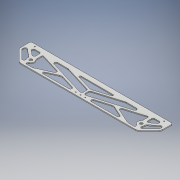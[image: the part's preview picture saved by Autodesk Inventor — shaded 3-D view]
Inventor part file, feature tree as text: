
AUTODESK INVENTOR PART (.ipt)
format: ipt  version: 2018.3 (Build 223284000, 284)  size: 371,712 bytes
history: native  units: mm
features: fillet x20, extrude x5, sketch x4
ambient origin geometry x8: Origin, YZ Plane, XZ Plane, XY Plane, X Axis, Y Axis, Z Axis, Center Point
bodies: Solid1 (feature_tree)
feature tree (29):
  sketch  "Sketch1"  dims[d14=6.0mm d18=6.0mm d19=6.0mm d22=6.0mm d26=37.5mm]
  extrude  "Extrusion1"  Depth=37.5mm
  extrude  "Extrusion2"  Depth=37.5mm
  fillet  "Fillet1"  Radius=3.1mm
  fillet  "Fillet2"  Radius=7.5mm
  fillet  "Fillet3"  Radius=3.1mm
  fillet  "Fillet5"  Radius=7.5mm
  fillet  "Fillet6"  Radius=6.0mm
  fillet  "Fillet7"  Radius=6.0mm
  fillet  "Fillet8"  Radius=3.0mm
  fillet  "Fillet9"  Radius=3.0mm
  fillet  "Fillet10"  Radius=3.0mm
  fillet  "Fillet11"  Radius=3.175mm
  fillet  "Fillet12"  Radius=3.175mm
  extrude  "Extrusion3"  Depth=15.0mm
  fillet  "Fillet13"  Radius=15.0mm
  fillet  "Fillet14"  Radius=10.0mm
  fillet  "Fillet15"  Radius=5.0mm
  fillet  "Fillet16"  Radius=5.0mm
  fillet  "Fillet17"  Radius=5.0mm
  fillet  "Fillet18"  Radius=5.0mm
  fillet  "Fillet19"  Radius=3.0mm
  fillet  "Fillet20"  Radius=3.0mm
  extrude  "Extrusion4"  Depth=3.0mm
  fillet  "Fillet21"  Radius=3.175mm
  extrude  "Extrusion5"  Depth=12.0mm
  sketch  "Sketch2"  dims[d27=37.5mm d32=25.0mm d34=3.1mm d35=7.5mm d37=3.1mm d38=7.5mm]
  sketch  "Sketch3"  dims[d39=6.0mm d40=6.0mm d41=6.0mm d43=6.0mm d44=6.0mm d50=3.0mm d59=3.0mm d60=3.0mm d64=3.175mm d65=0.0mm d66=3.175mm d67=0.0mm]
  sketch  "Sketch4"  dims[d68=5.0mm d69=15.0mm d70=15.0mm d72=10.0mm d73=5.0mm d74=5.0mm d75=5.0mm d76=5.0mm d77=3.0mm d78=3.0mm d79=3.0mm d82=3.175mm d83=0.0mm d84=12.0mm d85=6.0mm d86=6.0mm d87=3.0mm d88=5.0mm d89=5.0mm d90=12.0mm d91=4.0mm d92=3.175mm d93=0.0mm d94=12.0mm d95=3.1mm d96=15.0mm d97=3.1mm d98=15.0mm d99=10.0mm d100=0.0mm]
